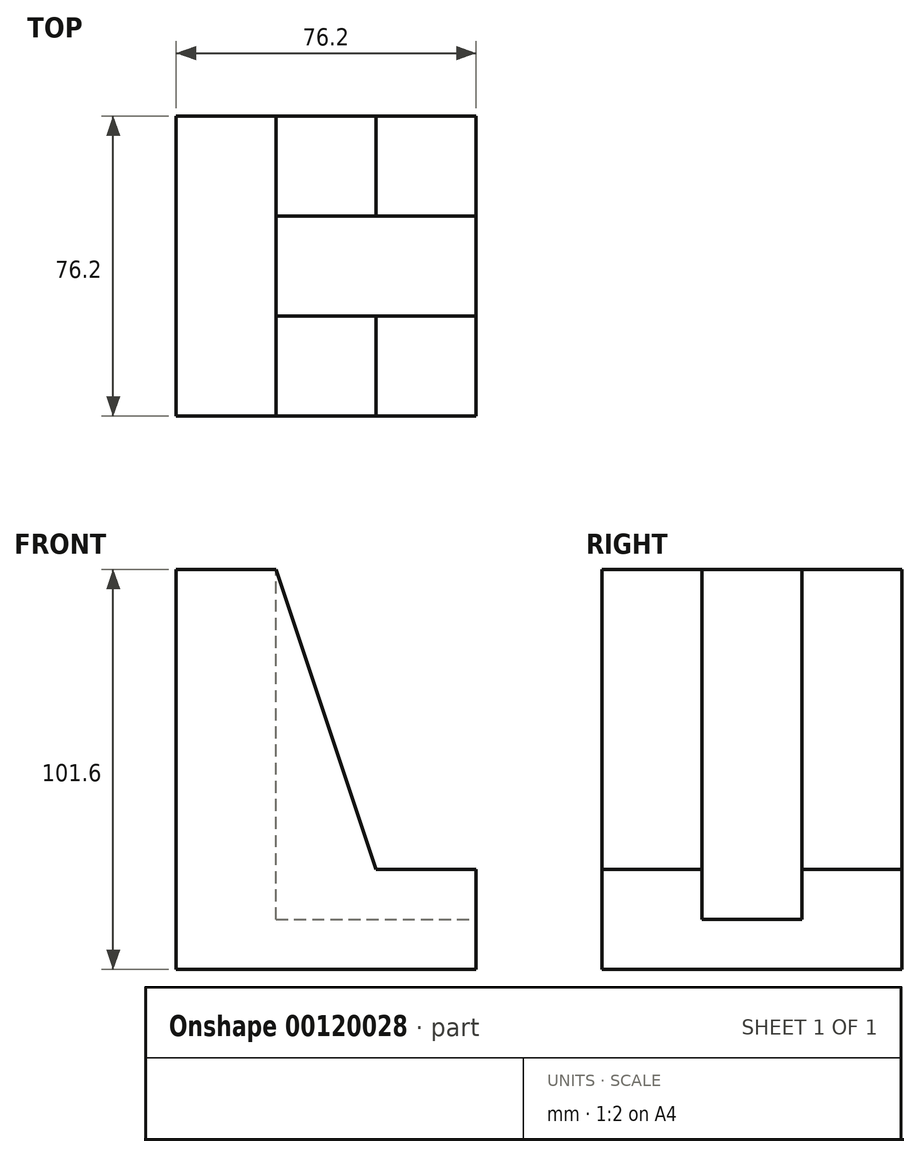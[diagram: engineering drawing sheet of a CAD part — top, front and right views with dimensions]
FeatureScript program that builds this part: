
annotation { "Feature Type Name" : "Feature", "Feature Type Description" : "" }
export const myFeature = defineFeature(function(context is Context, id is Id, definition is map)
    precondition{}
    {
        {
            var Q0;
            Q0=qCreatedBy(makeId("Front.planeOp"),FACE);
            var sketch = newSketch(context, id + "F0", { "sketchPlane" : qUnion([Q0])});
            skLineSegment(sketch, "E0", {"start": v(0, 0) * mm, "end": v(0, 101.6) * mm});
            skLineSegment(sketch, "E1", {"start": v(0, 101.6) * mm, "end": v(25.4, 101.6) * mm});
            skLineSegment(sketch, "E2", {"start": v(25.4, 101.6) * mm, "end": v(50.8, 25.4) * mm});
            skLineSegment(sketch, "E3", {"start": v(50.8, 25.4) * mm, "end": v(76.2, 25.4) * mm});
            skLineSegment(sketch, "E4", {"start": v(76.2, 25.4) * mm, "end": v(76.2, 0) * mm});
            skLineSegment(sketch, "E5", {"start": v(76.2, 0) * mm, "end": v(0, 0) * mm});
            skSolve(sketch);
        }
        {
            var Q0;
            Q0 = qSketchRegion(id + "F0", true);
            extrude(context, id + "F1", {"entities" : qUnion([Q0]), "depth" : 76.2 * mm});
        }
        {
            var Q0;
            Q0=makeQuery(id+"F1.opExtrude","SWEPT_FACE",FACE,{"disambiguationData":[OSD([sQuery(id+"F0.wireOp",EDGE,"E1")])]});
            var sketch = newSketch(context, id + "F2", { "sketchPlane" : qUnion([Q0])});
            skLineSegment(sketch, "E6.bottom", {"start": v(25.4, -25.4) * mm, "end": v(76.2, -25.4) * mm});
            skLineSegment(sketch, "E6.top", {"start": v(25.4, -50.8) * mm, "end": v(76.2, -50.8) * mm});
            skLineSegment(sketch, "E6.left", {"start": v(25.4, -25.4) * mm, "end": v(25.4, -50.8) * mm});
            skLineSegment(sketch, "E6.right", {"start": v(76.2, -25.4) * mm, "end": v(76.2, -50.8) * mm});
            skSolve(sketch);
        }
        {
            var Q0;
            Q0=makeQuery(id+"F2.imprint","IMPRINT",FACE,{"disambiguationData":[TD([[makeQuery(id+"F2.imprint","IMPRINT",EDGE,{"derivedFrom":sQuery(id+"F2.wireOp",EDGE,"E6.bottom")}),-1.0]])]});
            extrude(context, id + "F3", {"entities" : qUnion([Q0]), "operationType" : NewBodyOperationType.REMOVE, "oppositeDirection" : true, "depth" : 88.9 * mm});
        }
    });
